# Revit family: PRD_AR_PprTwlDspnsrs_RODANPaperTowelDispenser_RODX600E
name_source: partatom
category: Specialty Equipment
revit_build: Autodesk Revit 2018 (Build: 20190510_1515(x64)
units: mm (PartAtom-declared; Revit-internal decimal feet)

## family parameters
Cut with Voids When Loaded = Yes
Host = Face
OmniClass Number = 23.40.20.21.17
OmniClass Title = Paper Towel Dispensers, Disposal Units
Part Type = Normal
Room Calculation Point = No
Round Connector Dimension = Use Diameter
Shared = No

## types (1)
- RODX600E
    AssetType = Fixed
    BIMObjectName = PRD_AR_PaperTowelDispensers_RODANPaperTowelDispenser_RODX600E
    Category = Pr_40_70_22_62, Paper Towel Dispensers
    Default Elevation = 850 mm  [stored 2.78871 ft]
    Description = Paper towel dispenser for recessed mounting, stainless steel, surface satin finished, material thickness 0.8 mm, folded front cover, cylinder lock with KWC standard key, loading capacity 300 - 400 pcs. of paper depending on convolution, includes stainless steel screws and dowels.
    DispenserMaterial = PRD_AR_StainlessSteel_SatinFinished
    DurationUnit = year
    Features = stainless steel, surface satin finished
    FillingQuantity = 400
    FillingQuantityUom = Towels
    Finish = satin finished
    GrossWeight = 3.99 kg
    IfcExportAs = IfcFurnitureType
    IfcExportType = USERDEFINED
    IntegralAccessories = incl. stainless steel screws and dowels
    IsBuiltIn = TRUE
    Lock = Key-lock
    MainColor = stainless steel
    Manufacturer = KWC Group AG
    ManufacturerName = KWC Group AG
    ManufacturerURL = www.kwc.com
    Material = stainless steel
    MaterialCode = 1.4301
    MaterialThickness = 0.80 mm
    Model = RODX600E
    ModelNumber = 2000090057
    ModelReference = RODX600E
    NBSDescription = Paper towel dispensers
    NBSReference = 45-35-72/344
    Name = Paper Towel Dispenser RODX600E
    NetWeight = 3.39 kg
    NominalDepth = 112 mm  [stored 0.367454 ft]
    NominalHeight = 513 mm  [stored 1.68307 ft]
    NominalWidth = 324 mm  [stored 1.06299 ft]
    Offset = 0 mm  [stored 0 ft]
    ProductInformation = https://pim.kwc.com
    Size = 324 x 513 x 112 mm
    Style = Dispenser
    TypeOfConsumable = Paper towel
    TypeOfFixing = Screw
    TypeOfMounting = Recessed mounting
    TypeOfOperation = Manual operation
    URL = www.kwc.com
    Uniclass2015Code = Pr_40_70_22_62
    Uniclass2015Title = Paper towel dispensers
    Uniclass2015Version = Products v1.17
    Version = 1
    WarrantyDurationUnit = year

note: [stored X ft] marks values corroborated as IEEE doubles in the binary element streams (Revit-internal decimal feet)

## geometry (parser evidence)
native form markers: Sweep x3
no freeform markers — native parametric forms only
